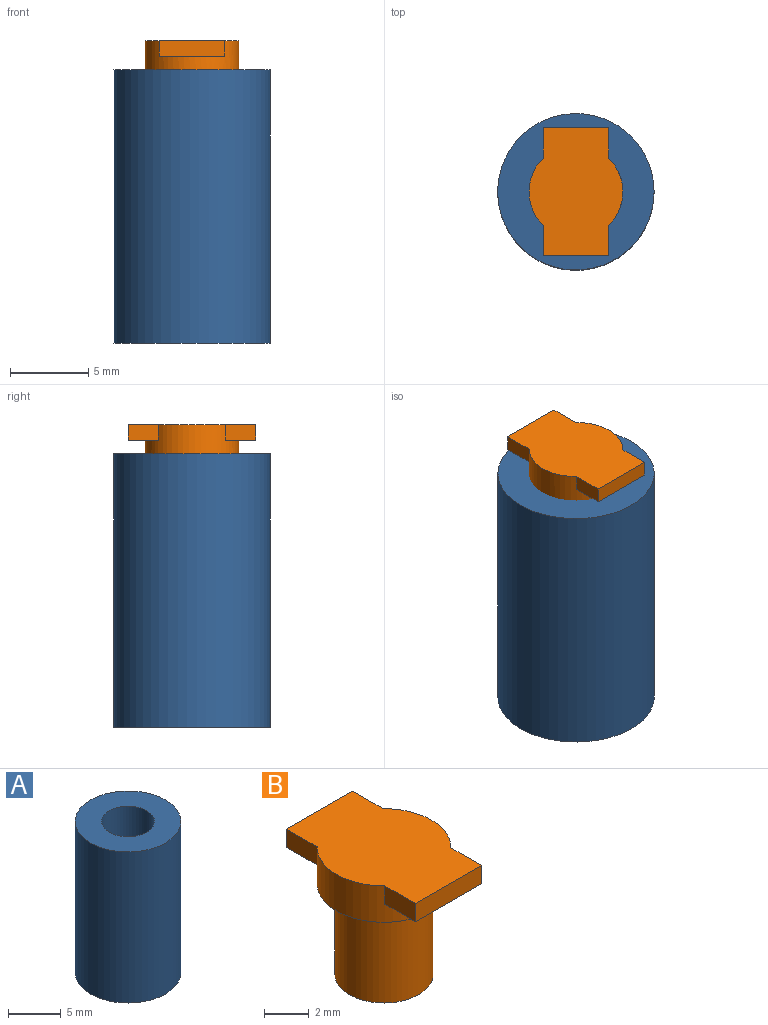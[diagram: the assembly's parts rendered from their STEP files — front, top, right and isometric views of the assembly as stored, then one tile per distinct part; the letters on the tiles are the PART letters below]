
ASSEMBLY  parts=2 mates=1
PART A: 6 faces, bbox 10x10x17.5 mm
  f0: plane 5x5mm, normal (0,0,1), area 15.1mm2, adj f1,f4
  f1: cylinder r=1.2mm len=10mm, axis (0,0,-1), area 75.4mm2, adj f0,f3
  f2: cylinder r=5mm len=17.5mm, axis (0,0,-1), area 549.8mm2, adj f3,f5
  f3: plane 10x10mm, normal (0,0,-1), area 74mm2, adj f1,f2
  f4: cylinder r=2.5mm len=7.5mm, axis (0,0,-1), area 117.8mm2, adj f0,f5
  f5: plane 10x10mm, normal (0,0,1), area 58.9mm2, adj f2,f4
PART B: 13 faces, bbox 6x8.2x7 mm
  f0: cylinder r=2.2mm len=5mm, axis (0,0,-1), area 69.1mm2, adj f1,f4
  f1: plane 4.4x4.4mm, normal (0,0,-1), area 15.2mm2, adj f0
  f2: cylinder r=3mm len=6mm, axis (0,0,-1), area 28.4mm2, adj f3,f4,f6,f7,f8,f9,f10,f11
  f3: plane 8.19x6mm, normal (0,0,1), area 39.6mm2, adj f2,f5,f7,f8,f10,f11,f12
  f4: plane 6x6mm, normal (0,0,-1), area 13.1mm2, adj f0,f2
  f5: plane 4.19x1mm, normal (0,-1,0), area 4.2mm2, adj f3,f6,f7,f8
  f6: plane 4.19x1.94mm, normal (0,0,-1), area 5.7mm2, adj f2,f5,f7,f8
  f7: plane 1.94x1mm, normal (1,0,0), area 1.9mm2, adj f2,f3,f5,f6
  f8: plane 1.94x1mm, normal (-1,0,0), area 1.9mm2, adj f2,f3,f5,f6
  f9: plane 4.19x1.94mm, normal (0,0,-1), area 5.7mm2, adj f2,f10,f11,f12
  f10: plane 1.94x1mm, normal (-1,0,0), area 1.9mm2, adj f2,f3,f9,f12
  f11: plane 1.94x1mm, normal (1,0,0), area 1.9mm2, adj f2,f3,f9,f12
  f12: plane 4.19x1mm, normal (0,1,0), area 4.2mm2, adj f3,f9,f10,f11
PLACE A t=(9.81,4.28,-33.85)mm fixed
PLACE B t=(9.81,4.28,-21.48)mm
MATE slider A.f4 <-> B.f0  axis (0,0,-1) through (9.81,4.28,-16.35)mm
